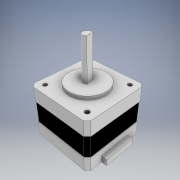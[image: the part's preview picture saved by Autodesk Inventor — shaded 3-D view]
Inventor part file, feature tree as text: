
AUTODESK INVENTOR PART (.ipt)
format: ipt  version: 2020 (Build 240168000, 168)  size: 202,240 bytes
history: native  units: mm
features: sketch x7, extrude x6, projected_geometry x2, hole x1
ambient origin geometry x8: Origin, YZ Plane, XZ Plane, XY Plane, X Axis, Y Axis, Z Axis, Center Point
bodies: Solid1 (feature_tree)
feature tree (16):
  extrude  "Extrusion1"  Depth=35.0mm
  extrude  "Extrusion2"  Depth=2.0mm
  extrude  "Extrusion3"  Depth=2.0mm
  extrude  "Extrusion4"  Depth=2.0mm
  extrude  "Extrusion5"  Depth=2.0mm
  hole  "Hole1"  [1 undecoded]
  extrude  "Extrusion6"  Depth=2.0mm
  sketch  "Sketch1"  dims[d0=35.0mm d1=35.0mm]
  sketch  "Sketch2"  dims[d2=2.0mm d3=2.0mm]
  projected_geometry  "Projected Loop1"
  sketch  "Sketch3"  dims[d4=2.0mm d5=2.0mm]
  projected_geometry  "Projected Loop2"
  sketch  "Sketch4"  dims[d6=2.0mm d7=2.0mm]
  sketch  "Sketch5"  dims[d8=2.0mm d9=2.0mm]
  sketch  "Sketch6"  dims[d10=8.0mm d11=0.0mm d12=34.5mm]
  sketch  "Sketch7"  dims[d13=34.5mm d14=2.0mm d15=2.0mm d16=2.0mm d17=2.0mm d18=2.0mm d19=2.0mm d20=2.0mm d21=2.0mm d22=12.0mm d23=0.0mm d24=8.0mm d25=0.0mm d26=22.0mm d27=2.0mm d28=0.0mm d29=5.0mm d30=22.0mm d31=0.0mm d32=26.0mm d33=26.0mm d34=4.5mm d35=4.5mm d36=2.459mm d37=6.0mm d38=6.0mm d39=2.0mm d40=90.0deg d41=8.8mm d42=20.594885mm d43=3.0mm d44=0.0mm d45=4.5mm d46=4.5mm d47=4.5mm d48=4.5mm d49=4.5mm]
note: 1 required parameter value undecoded (feature->parameter linkage not recoverable at this tier; creation-order binding heuristic only, values carry confidence <= 0.55)
